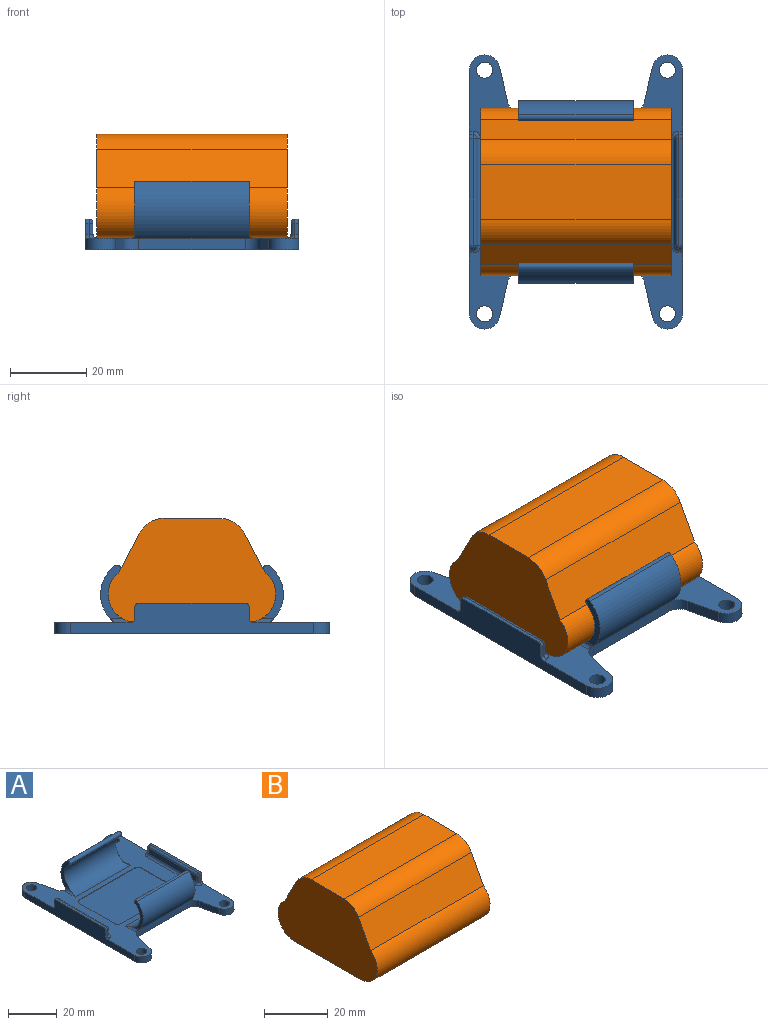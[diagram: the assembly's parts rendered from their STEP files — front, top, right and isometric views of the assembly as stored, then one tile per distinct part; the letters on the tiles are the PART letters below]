
ASSEMBLY  parts=2 mates=1
PART A: 77 faces, bbox 56x72x18 mm
  f0: plane 9.4x3mm, normal (-0.97,0.23,0), area 29mm2, adj f5,f28,f61,f62
  f1: plane 9.4x3mm, normal (0.97,-0.23,0), area 29mm2, adj f5,f28,f66,f67
  f2: plane 9.4x3mm, normal (0.97,0.23,0), area 29mm2, adj f4,f5,f28,f59
  f3: plane 9.4x3mm, normal (-0.97,-0.23,0), area 29mm2, adj f5,f6,f28,f64
  f4: cylinder r=4mm len=3.89mm, axis (0,0,-1), area 16.1mm2, adj f2,f5,f28,f48,f60
  f5: plane 72x56mm, normal (0,0,-1), area 2779.5mm2, adj f0,f1,f2,f3,f4,f6,f59,f60
  f6: cylinder r=4mm len=3.89mm, axis (0,0,-1), area 16.1mm2, adj f3,f5,f28,f55,f65
  f7: cylinder r=2mm len=2mm, axis (0,0,-1), area 0.8mm2, adj f8,f14,f15,f28
  f8: plane 20x0.25mm, normal (-1,0,0), area 5mm2, adj f7,f9,f15,f28
  f9: cylinder r=2mm len=2mm, axis (0,0,-1), area 0.8mm2, adj f8,f10,f15,f28
  f10: plane 32x0.25mm, normal (0,-1,0), area 8mm2, adj f9,f11,f15,f28
  f11: cylinder r=2mm len=2mm, axis (0,0,-1), area 0.8mm2, adj f10,f12,f15,f28
  f12: plane 20x0.25mm, normal (1,0,0), area 5mm2, adj f11,f13,f15,f28
  f13: cylinder r=2mm len=2mm, axis (0,0,-1), area 0.8mm2, adj f12,f14,f15,f28
  f14: plane 32x0.25mm, normal (0,1,0), area 8mm2, adj f7,f13,f15,f28
  f15: plane 36x24mm, normal (0,0,1), area 860.6mm2, adj f7,f8,f9,f10,f11,f12,f13,f14
  f16: sphere r=1mm, area 1.5mm2, adj f25,f26,f27
  f17: torus R=2mm, axis (0,0,-1), area 3.4mm2, adj f18,f23,f26,f28
  f18: cylinder r=1mm len=1mm, axis (1,0,0), area 1.6mm2, adj f17,f28,f29,f63
  f19: sphere r=1mm, area 1.5mm2, adj f22,f24,f25
  f20: torus R=2mm, axis (0,0,1), area 3.4mm2, adj f21,f22,f23,f28
  f21: cylinder r=1mm len=1mm, axis (-1,0,0), area 1.6mm2, adj f20,f28,f63,f72
  f22: cylinder r=1mm len=3mm, axis (0,0,1), area 4.7mm2, adj f19,f20,f30,f72
  f23: cylinder r=1mm len=28mm, axis (0,1,0), area 44mm2, adj f17,f20,f28,f30
  f24: cylinder r=1mm len=1mm, axis (1,0,0), area 1.6mm2, adj f19,f63,f72,f73
  f25: cylinder r=1mm len=28mm, axis (0,-1,0), area 44mm2, adj f16,f19,f30,f73
  f26: cylinder r=1mm len=3mm, axis (0,0,1), area 4.7mm2, adj f16,f17,f29,f30
  f27: cylinder r=1mm len=1mm, axis (-1,0,0), area 1.6mm2, adj f16,f29,f63,f73
  f28: plane 72x56mm, normal (0,0,1), area 1360.5mm2, adj f0,f1,f2,f3,f4,f6,f7,f8
  f29: plane 3x1mm, normal (0,1,0), area 3mm2, adj f18,f26,f27,f63
  f30: plane 28x3mm, normal (-1,0,0), area 84mm2, adj f22,f23,f25,f26
  f31: sphere r=1mm, area 1.4mm2, adj f39,f40,f42
  f32: torus R=2mm, axis (0,0,1), area 3.4mm2, adj f28,f35,f40,f41
  f33: sphere r=1mm, area 1.6mm2, adj f37,f38,f39
  f34: torus R=2mm, axis (0,0,-1), area 3.4mm2, adj f28,f35,f36,f37
  f35: cylinder r=1mm len=28mm, axis (0,-1,0), area 44mm2, adj f28,f32,f34,f44
  f36: cylinder r=1mm len=1mm, axis (1,0,0), area 1.6mm2, adj f28,f34,f43,f75
  f37: cylinder r=1mm len=3mm, axis (0,0,1), area 4.7mm2, adj f33,f34,f43,f44
  f38: cylinder r=1mm len=1mm, axis (-1,0,0), area 1.6mm2, adj f33,f43,f75,f76
  f39: cylinder r=1mm len=28mm, axis (0,1,0), area 44mm2, adj f31,f33,f44,f76
  f40: cylinder r=1mm len=3mm, axis (0,0,1), area 4.7mm2, adj f31,f32,f44,f74
  f41: cylinder r=1mm len=1mm, axis (-1,0,0), area 1.6mm2, adj f28,f32,f74,f75
  f42: cylinder r=1mm len=1mm, axis (1,0,0), area 1.6mm2, adj f31,f74,f75,f76
  f43: plane 3x1mm, normal (0,1,0), area 3mm2, adj f36,f37,f38,f75
  f44: plane 28x3mm, normal (1,0,0), area 84mm2, adj f35,f37,f39,f40
  f45: cylinder r=1mm len=6.86mm, axis (0,-1,0), area 7mm2, adj f28,f48,f50,f51
  f46: cylinder r=1mm len=6.86mm, axis (0,1,0), area 7mm2, adj f28,f47,f48,f50
  f47: plane 14.03x5.65mm, normal (-1,0,0), area 31.6mm2, adj f46,f48,f49,f50
  f48: cylinder r=9.35mm len=32mm, axis (1,0,0), area 514.4mm2, adj f4,f28,f45,f46,f47,f49,f51,f60
  f49: cylinder r=1mm len=30mm, axis (1,0,0), area 94.2mm2, adj f47,f48,f50,f51
  f50: cylinder r=7.35mm len=32mm, axis (1,0,0), area 554.7mm2, adj f28,f45,f46,f47,f49,f51
  f51: plane 14.03x5.65mm, normal (1,0,0), area 31.6mm2, adj f45,f48,f49,f50
  f52: cylinder r=1mm len=6.86mm, axis (0,-1,0), area 7mm2, adj f28,f53,f55,f58
  f53: plane 14.03x5.65mm, normal (1,0,0), area 31.6mm2, adj f52,f55,f57,f58
  f54: cylinder r=1mm len=6.86mm, axis (0,1,0), area 7mm2, adj f28,f55,f56,f58
  f55: cylinder r=9.35mm len=32mm, axis (-1,0,0), area 514.4mm2, adj f6,f28,f52,f53,f54,f56,f57,f65
  f56: plane 14.03x5.65mm, normal (-1,0,0), area 31.6mm2, adj f54,f55,f57,f58
  f57: cylinder r=1mm len=30mm, axis (-1,0,0), area 94.2mm2, adj f53,f55,f56,f58
  f58: cylinder r=7.35mm len=32mm, axis (-1,0,0), area 554.7mm2, adj f28,f52,f53,f54,f56,f57
  f59: cylinder r=4mm len=7.89mm, axis (0,0,1), area 34.9mm2, adj f2,f5,f28,f75
  f60: plane 28x3mm, normal (0,1,0), area 84mm2, adj f4,f5,f48,f61
  f61: cylinder r=4mm len=3.89mm, axis (0,0,-1), area 16.1mm2, adj f0,f5,f28,f48,f60
  f62: cylinder r=4mm len=7.89mm, axis (0,0,1), area 34.9mm2, adj f0,f5,f28,f63
  f63: plane 64x8mm, normal (1,0,0), area 342mm2, adj f5,f18,f21,f24,f27,f28,f29,f62
  f64: cylinder r=4mm len=7.89mm, axis (0,0,1), area 34.9mm2, adj f3,f5,f28,f63
  f65: plane 28x3mm, normal (0,-1,0), area 84mm2, adj f5,f6,f55,f66
  f66: cylinder r=4mm len=3.89mm, axis (0,0,-1), area 16.1mm2, adj f1,f5,f28,f55,f65
  f67: cylinder r=4mm len=7.89mm, axis (0,0,1), area 34.9mm2, adj f1,f5,f28,f75
  f68: cylinder r=2.1mm len=4.2mm, axis (0,0,1), area 39.6mm2, adj f5,f28
  f69: cylinder r=2.1mm len=4.2mm, axis (0,0,1), area 39.6mm2, adj f5,f28
  f70: cylinder r=2.1mm len=4.2mm, axis (0,0,1), area 39.6mm2, adj f5,f28
  f71: cylinder r=2.1mm len=4.2mm, axis (0,0,1), area 39.6mm2, adj f5,f28
  f72: plane 3x1mm, normal (0,-1,0), area 3mm2, adj f21,f22,f24,f63
  f73: plane 28x1mm, normal (0,0,1), area 28mm2, adj f24,f25,f27,f63
  f74: plane 3x1mm, normal (0,-1,0), area 3mm2, adj f40,f41,f42,f75
  f75: plane 64x8mm, normal (-1,0,0), area 342mm2, adj f5,f28,f36,f38,f41,f42,f43,f59
  f76: plane 28x1mm, normal (0,0,1), area 28mm2, adj f38,f39,f42,f75
PART B: 10 faces, bbox 50x44x27.3 mm
  f0: cylinder r=7.3mm len=50mm, axis (-1,0,0), area 397.4mm2, adj f1,f7,f8,f9
  f1: plane 50x10.16mm, normal (0,-0.89,0.46), area 573.5mm2, adj f0,f2,f8,f9
  f2: cylinder r=7.35mm len=50mm, axis (-1,0,0), area 918mm2, adj f1,f3,f8,f9
  f3: plane 50x29.3mm, normal (0,0,-1), area 1465mm2, adj f2,f4,f8,f9
  f4: cylinder r=7.35mm len=50mm, axis (-1,0,0), area 918mm2, adj f3,f5,f8,f9
  f5: plane 50x10.16mm, normal (0,0.89,0.46), area 571.8mm2, adj f4,f6,f8,f9
  f6: cylinder r=7.3mm len=50mm, axis (-1,0,0), area 400.7mm2, adj f5,f7,f8,f9
  f7: plane 50x14.57mm, normal (0,0,1), area 728.6mm2, adj f0,f6,f8,f9
  f8: plane 44x27.34mm, normal (1,0,0), area 975.9mm2, adj f0,f1,f2,f3,f4,f5,f6,f7
  f9: plane 44x27.34mm, normal (-1,0,0), area 975.9mm2, adj f0,f1,f2,f3,f4,f5,f6,f7
PLACE A t=(-27.37,-10.26,8.93)mm
PLACE B t=(-16.37,-10.26,8.93)mm
MATE fastened B.f2 <-> A.f55  axis (1,0,0) through (33.63,3.09,17.78)mm
